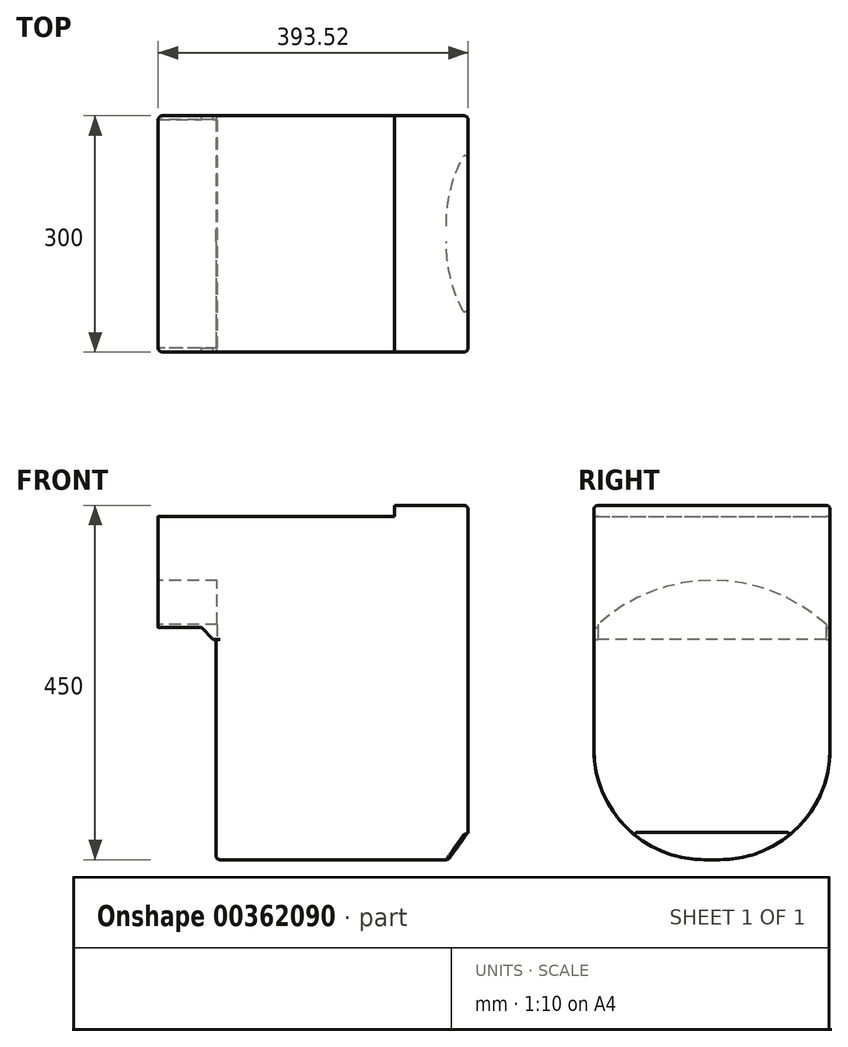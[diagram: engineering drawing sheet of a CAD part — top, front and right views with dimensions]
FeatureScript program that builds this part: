
annotation { "Feature Type Name" : "Feature", "Feature Type Description" : "" }
export const myFeature = defineFeature(function(context is Context, id is Id, definition is map)
    precondition{}
    {
        {
            var Q0;
            Q0=qCreatedBy(makeId("Front.planeOp"),FACE);
            var sketch = newSketch(context, id + "F0", { "sketchPlane" : qUnion([Q0])});
            skLineSegment(sketch, "E0", {"start": v(-209.31, 94.65) * mm, "end": v(90.62, 94.65) * mm});
            skLineSegment(sketch, "E1", {"start": v(90.62, 94.65) * mm, "end": v(90.62, 74.54) * mm});
            skLineSegment(sketch, "E2", {"start": v(90.62, 74.54) * mm, "end": v(99.04, 67) * mm});
            skLineSegment(sketch, "E3", {"start": v(99.04, 67) * mm, "end": v(125.16, 67) * mm});
            skLineSegment(sketch, "E4", {"start": v(125.16, 67) * mm, "end": v(125.16, -341.57) * mm});
            skLineSegment(sketch, "E5", {"start": v(90.62, 94.65) * mm, "end": v(90.62, 108.43) * mm});
            skLineSegment(sketch, "E6", {"start": v(90.62, 108.43) * mm, "end": v(184.21, 108.43) * mm});
            skLineSegment(sketch, "E7", {"start": v(184.21, 108.43) * mm, "end": v(184.21, -306.92) * mm});
            skLineSegment(sketch, "E8", {"start": v(-135.79, -341.57) * mm, "end": v(234.39, -341.57) * mm});
            skLineSegment(sketch, "E9", {"start": v(159.12, -341.57) * mm, "end": v(184.21, -306.92) * mm});
            skLineSegment(sketch, "E10", {"start": v(-135.79, -341.57) * mm, "end": v(-135.79, -61.83) * mm});
            skLineSegment(sketch, "E11", {"start": v(-135.79, -61.83) * mm, "end": v(-139.43, -61.83) * mm});
            skLineSegment(sketch, "E12", {"start": v(-154.47, -46.76) * mm, "end": v(-139.43, -61.83) * mm});
            skPoint(sketch, "E12.startSnap0", {"position": v(-154.47, -61.83) * mm});
            skLineSegment(sketch, "E13", {"start": v(-154.47, -46.76) * mm, "end": v(-209.31, -46.76) * mm});
            skLineSegment(sketch, "E14", {"start": v(-209.31, 94.65) * mm, "end": v(-209.31, -46.76) * mm});
            skPoint(sketch, "E15.end.orphan", {"position": v(-173.15, 258.04) * mm});
            skPoint(sketch, "E16.orphan", {"position": v(-209.31, 108.43) * mm});
            skPoint(sketch, "E17.orphan", {"position": v(90.62, 132.04) * mm});
            skPoint(sketch, "E18.orphan", {"position": v(-173.15, -61.83) * mm});
            skSolve(sketch);
        }
        {
            var Q0;
            Q0=makeQuery(id+"F0.imprint","IMPRINT",FACE,{"disambiguationData":[TD([[makeQuery(id+"F0.imprint","IMPRINT",EDGE,{"derivedFrom":sQuery(id+"F0.wireOp",EDGE,"E0")}),-1.0]])]});
            var Q1;
            Q1=makeQuery(id+"F0.imprint","IMPRINT",FACE,{"disambiguationData":[TD([[makeQuery(id+"F0.imprint","IMPRINT",EDGE,{"derivedFrom":sQuery(id+"F0.wireOp",EDGE,"E1")}),1.0]])]});
            extrude(context, id + "F1", {"entities" : qUnion([Q0, Q1]), "depth" : 300 * mm});
        }
        {
            var Q0;
            Q0=makeQuery(id+"F1.opExtrude","SWEPT_EDGE",EDGE,{"disambiguationData":[OSD([sQuery(id+"F0.wireOp",EDGE,"E6"),sQuery(id+"F0.wireOp",EDGE,"E7")])]});
            var Q1;
            Q1=makeQuery(id+"F1.opExtrude","CAP_EDGE",EDGE,{"disambiguationData":[OSD([sQuery(id+"F0.wireOp",EDGE,"E7")])],"isStart":false});
            var Q2;
            Q2=makeQuery(id+"F1.opExtrude","CAP_EDGE",EDGE,{"disambiguationData":[OSD([sQuery(id+"F0.wireOp",EDGE,"E7")])],"isStart":true});
            var Q3;
            Q3=makeQuery(id+"F1.opExtrude","CAP_EDGE",EDGE,{"disambiguationData":[OSD([sQuery(id+"F0.wireOp",EDGE,"E14")])],"isStart":false});
            var Q4;
            Q4=makeQuery(id+"F1.opExtrude","CAP_EDGE",EDGE,{"disambiguationData":[OSD([sQuery(id+"F0.wireOp",EDGE,"E14")])],"isStart":true});
            fillet(context, id + "F2", {"entities" : qUnion([Q0, Q1, Q2, Q3, Q4]), "radius" : 5 * mm, "tangentPropagation" : true, "allowEdgeOverflow" : false});
        }
        {
            var Q0;
            Q0=makeQuery(id+"F1.opExtrude","CAP_EDGE",EDGE,{"disambiguationData":[OSD([sQuery(id+"F0.wireOp",EDGE,"E8")])],"isStart":false});
            var Q1;
            Q1=makeQuery(id+"F1.opExtrude","CAP_EDGE",EDGE,{"disambiguationData":[OSD([sQuery(id+"F0.wireOp",EDGE,"E8")])],"isStart":true});
            fillet(context, id + "F3", {"entities" : qUnion([Q0, Q1]), "radius" : 140 * mm, "tangentPropagation" : true, "allowEdgeOverflow" : false});
        }
        {
            var Q0;
            Q0=makeQuery(id+"F3.opFillet","BLEND_EDGE",EDGE,{"blendedFrom":[makeQuery(id+"F1.opExtrude","CAP_EDGE",EDGE,{"disambiguationData":[OSD([sQuery(id+"F0.wireOp",EDGE,"E8")])],"isStart":false}),makeQuery(id+"F1.opExtrude","SWEPT_FACE",FACE,{"disambiguationData":[OSD([sQuery(id+"F0.wireOp",EDGE,"E7")])]})],"blendedInto":[makeQuery(id+"F1.opExtrude","SWEPT_FACE",FACE,{"disambiguationData":[OSD([sQuery(id+"F0.wireOp",EDGE,"E7")])]})]});
            var Q1;
            Q1=makeQuery(id+"F3.opFillet","BLEND_EDGE",EDGE,{"blendedFrom":[makeQuery(id+"F1.opExtrude","CAP_EDGE",EDGE,{"disambiguationData":[OSD([sQuery(id+"F0.wireOp",EDGE,"E8")])],"isStart":false}),makeQuery(id+"F1.opExtrude","SWEPT_FACE",FACE,{"disambiguationData":[OSD([sQuery(id+"F0.wireOp",EDGE,"E9")])]})],"blendedInto":[makeQuery(id+"F1.opExtrude","SWEPT_FACE",FACE,{"disambiguationData":[OSD([sQuery(id+"F0.wireOp",EDGE,"E9")])]})]});
            var Q2;
            Q2=makeQuery(id+"F3.opFillet","BLEND_EDGE",EDGE,{"blendedFrom":[makeQuery(id+"F1.opExtrude","CAP_EDGE",EDGE,{"disambiguationData":[OSD([sQuery(id+"F0.wireOp",EDGE,"E8")])],"isStart":true}),makeQuery(id+"F1.opExtrude","SWEPT_FACE",FACE,{"disambiguationData":[OSD([sQuery(id+"F0.wireOp",EDGE,"E9")])]})],"blendedInto":[makeQuery(id+"F1.opExtrude","SWEPT_FACE",FACE,{"disambiguationData":[OSD([sQuery(id+"F0.wireOp",EDGE,"E9")])]})]});
            var Q3;
            Q3=makeQuery(id+"F1.opExtrude","SWEPT_EDGE",EDGE,{"disambiguationData":[OSD([sQuery(id+"F0.wireOp",EDGE,"E8"),sQuery(id+"F0.wireOp",EDGE,"E9")])]});
            var Q4;
            Q4=makeQuery(id+"F3.opFillet","BLEND_EDGE",EDGE,{"blendedFrom":[makeQuery(id+"F1.opExtrude","CAP_EDGE",EDGE,{"disambiguationData":[OSD([sQuery(id+"F0.wireOp",EDGE,"E8")])],"isStart":true}),makeQuery(id+"F1.opExtrude","SWEPT_FACE",FACE,{"disambiguationData":[OSD([sQuery(id+"F0.wireOp",EDGE,"E7")])]})],"blendedInto":[makeQuery(id+"F1.opExtrude","SWEPT_FACE",FACE,{"disambiguationData":[OSD([sQuery(id+"F0.wireOp",EDGE,"E7")])]})]});
            var Q5;
            Q5=makeQuery(id+"F3.opFillet","BLEND_EDGE",EDGE,{"blendedFrom":[makeQuery(id+"F1.opExtrude","CAP_EDGE",EDGE,{"disambiguationData":[OSD([sQuery(id+"F0.wireOp",EDGE,"E8")])],"isStart":true}),makeQuery(id+"F1.opExtrude","SWEPT_FACE",FACE,{"disambiguationData":[OSD([sQuery(id+"F0.wireOp",EDGE,"E10")])]})],"blendedInto":[makeQuery(id+"F1.opExtrude","SWEPT_FACE",FACE,{"disambiguationData":[OSD([sQuery(id+"F0.wireOp",EDGE,"E10")])]})]});
            var Q6;
            Q6=makeQuery(id+"F3.opFillet","BLEND_EDGE",EDGE,{"blendedFrom":[makeQuery(id+"F1.opExtrude","CAP_EDGE",EDGE,{"disambiguationData":[OSD([sQuery(id+"F0.wireOp",EDGE,"E8")])],"isStart":false}),makeQuery(id+"F1.opExtrude","SWEPT_FACE",FACE,{"disambiguationData":[OSD([sQuery(id+"F0.wireOp",EDGE,"E10")])]})],"blendedInto":[makeQuery(id+"F1.opExtrude","SWEPT_FACE",FACE,{"disambiguationData":[OSD([sQuery(id+"F0.wireOp",EDGE,"E10")])]})]});
            var Q7;
            Q7=makeQuery(id+"F1.opExtrude","SWEPT_EDGE",EDGE,{"disambiguationData":[OSD([sQuery(id+"F0.wireOp",EDGE,"E8"),sQuery(id+"F0.wireOp",EDGE,"E10")])]});
            fillet(context, id + "F4", {"entities" : qUnion([Q0, Q1, Q2, Q3, Q4, Q5, Q6, Q7]), "radius" : 5 * mm, "tangentPropagation" : true, "allowEdgeOverflow" : false});
        }
        {
            var Q0;
            Q0=makeQuery(id+"F1.opExtrude","CAP_EDGE",EDGE,{"disambiguationData":[OSD([sQuery(id+"F0.wireOp",EDGE,"E6")])],"isStart":false});
            var Q1;
            Q1=makeQuery(id+"F1.opExtrude","CAP_EDGE",EDGE,{"disambiguationData":[OSD([sQuery(id+"F0.wireOp",EDGE,"E6")])],"isStart":true});
            fillet(context, id + "F5", {"entities" : qUnion([Q0, Q1]), "radius" : 5 * mm, "tangentPropagation" : true, "allowEdgeOverflow" : false});
        }
        {
            var Q0;
            Q0=makeQuery(id+"F1.opExtrude","SWEPT_FACE",FACE,{"disambiguationData":[OSD([sQuery(id+"F0.wireOp",EDGE,"E14")])]});
            var sketch = newSketch(context, id + "F6", { "sketchPlane" : qUnion([Q0])});
            skArc(sketch, "E19", {"start": v(295, -42.72) * mm, "mid": v(150, 13.2) * mm, "end": v(5, -42.72) * mm});
            skPoint(sketch, "E19.centerSnap0", {"position": v(150, -46.76) * mm});
            skLineSegment(sketch, "E20", {"start": v(5, -46.76) * mm, "end": v(5, -61.87) * mm});
            skLineSegment(sketch, "E21", {"start": v(5, -61.87) * mm, "end": v(295, -61.87) * mm});
            skLineSegment(sketch, "E22", {"start": v(295, -61.87) * mm, "end": v(295, -46.76) * mm});
            skLineSegment(sketch, "E23", {"start": v(295, -46.76) * mm, "end": v(295, -42.72) * mm});
            skLineSegment(sketch, "E24", {"start": v(5, -46.76) * mm, "end": v(5, -42.72) * mm});
            skSolve(sketch);
        }
        {
            var Q0;
            Q0=makeQuery(id+"F6.imprint","IMPRINT",FACE,{"disambiguationData":[TD([[makeQuery(id+"F6.imprint","IMPRINT",EDGE,{"derivedFrom":sQuery(id+"F6.wireOp",EDGE,"E19")}),1.0]])]});
            var Q1;
            Q1=makeQuery(id+"F6.imprint","IMPRINT",FACE,{"disambiguationData":[TD([[makeQuery(id+"F6.imprint","IMPRINT",EDGE,{"derivedFrom":sQuery(id+"F6.wireOp",EDGE,"E20")}),1.0]])]});
            extrude(context, id + "F7", {"entities" : qUnion([Q0, Q1]), "operationType" : NewBodyOperationType.REMOVE, "oppositeDirection" : true, "depth" : 75 * mm});
        }
    });
